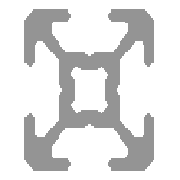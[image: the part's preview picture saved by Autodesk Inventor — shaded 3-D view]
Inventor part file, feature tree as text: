
AUTODESK INVENTOR PART (.ipt)
format: ipt  version: 2015 (Build 190159000, 159)  size: 377,856 bytes
history: native  units: mm
features: other x3, extrude x1, sketch x1
ambient origin geometry x8: Origin, YZ Plane, XZ Plane, XY Plane, X Axis, Y Axis, Z Axis, Center Point
bodies: Body1 (feature_tree)
feature tree (5):
  other  "Blocks"
  extrude  "Extrusion3"  [1 undecoded]
  sketch  "Sketch1"  dims[d23=0.0mm]
  other  "20x20"
  other  "20x20:1"
note: 1 required parameter value undecoded (feature->parameter linkage not recoverable at this tier; creation-order binding heuristic only, values carry confidence <= 0.55)
